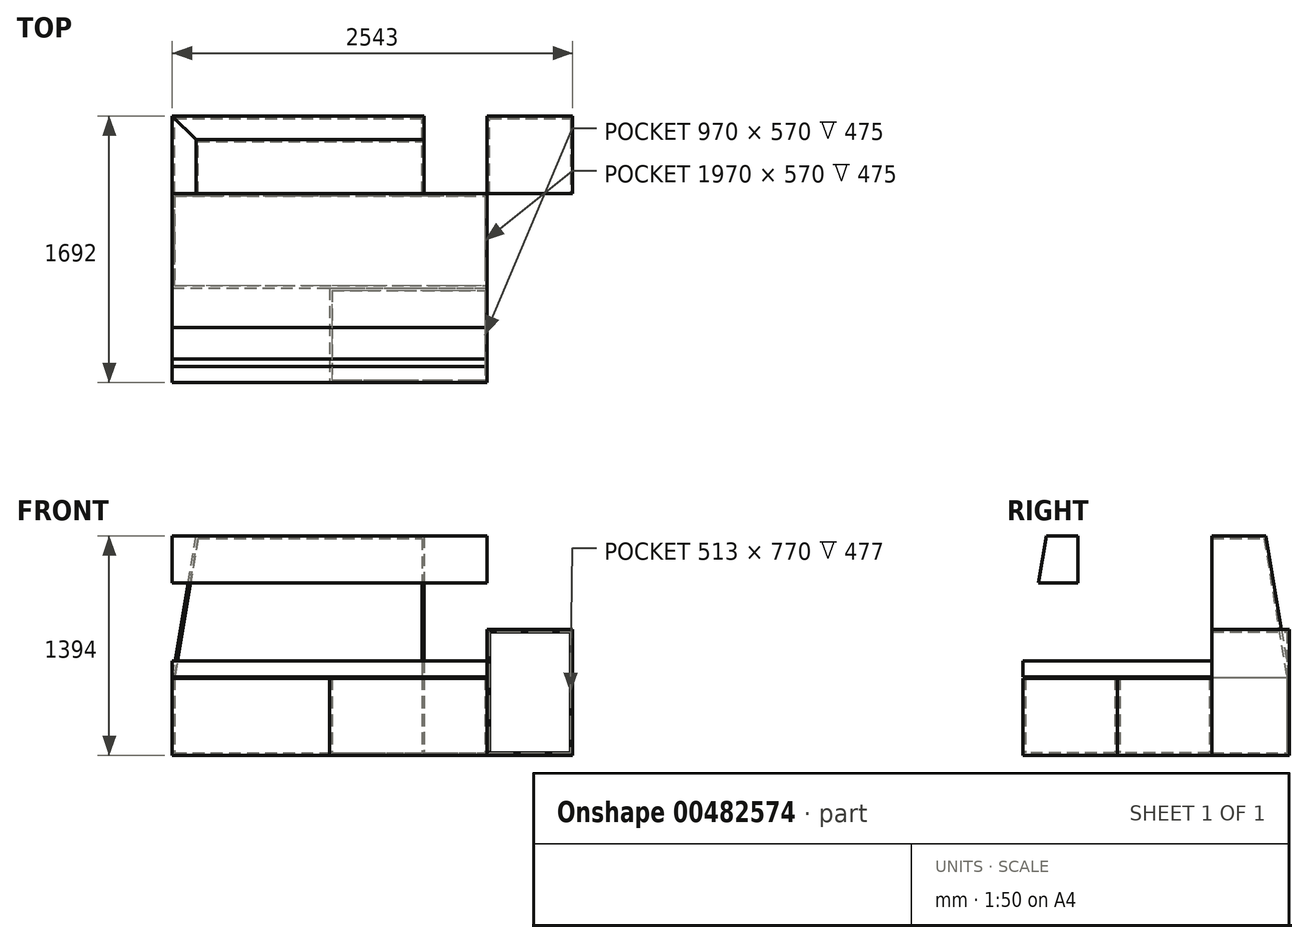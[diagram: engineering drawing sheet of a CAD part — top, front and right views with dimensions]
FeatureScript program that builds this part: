
annotation { "Feature Type Name" : "Feature", "Feature Type Description" : "" }
export const myFeature = defineFeature(function(context is Context, id is Id, definition is map)
    precondition{}
    {
        {
            var Q0;
            Q0=qCreatedBy(makeId("Top.planeOp"),FACE);
            var sketch = newSketch(context, id + "F0", { "sketchPlane" : qUnion([Q0])});
            skLineSegment(sketch, "E0.bottom", {"start": v(1471.5, -846) * mm, "end": v(-1471.5, -846) * mm, "construction": true});
            skLineSegment(sketch, "E0.top", {"start": v(1471.5, 846) * mm, "end": v(-1471.5, 846) * mm, "construction": true});
            skLineSegment(sketch, "E0.left", {"start": v(1471.5, -846) * mm, "end": v(1471.5, 846) * mm, "construction": true});
            skLineSegment(sketch, "E0.right", {"start": v(-1471.5, -846) * mm, "end": v(-1471.5, 846) * mm, "construction": true});
            skLineSegment(sketch, "E1", {"start": v(1071.5, 846) * mm, "end": v(1071.5, -846) * mm, "construction": true});
            skPoint(sketch, "E2", {"position": v(-1471.5, 622) * mm});
            skPoint(sketch, "E3", {"position": v(-1471.5, -622) * mm});
            skPoint(sketch, "E4", {"position": v(-1471.5, 0) * mm});
            skSolve(sketch);
        }
        {
            var Q0;
            Q0=qCreatedBy(makeId("Top.planeOp"),FACE);
            var sketch = newSketch(context, id + "F1", { "sketchPlane" : qUnion([Q0])});
            skLineSegment(sketch, "E5.bottom", {"start": v(-1471.5, 354) * mm, "end": v(528.5, 354) * mm});
            skLineSegment(sketch, "E5.top", {"start": v(-1471.5, -846) * mm, "end": v(528.5, -846) * mm});
            skLineSegment(sketch, "E5.left", {"start": v(-1471.5, 354) * mm, "end": v(-1471.5, -846) * mm});
            skLineSegment(sketch, "E5.right", {"start": v(528.5, 354) * mm, "end": v(528.5, -846) * mm});
            skLineSegment(sketch, "E6.top", {"start": v(-1471.5, 846) * mm, "end": v(528.5, 846) * mm});
            skLineSegment(sketch, "E6.left", {"start": v(-1471.5, 354) * mm, "end": v(-1471.5, 846) * mm});
            skLineSegment(sketch, "E6.right", {"start": v(528.5, 354) * mm, "end": v(528.5, 846) * mm});
            skLineSegment(sketch, "E7.left", {"start": v(-1471.5, -846) * mm, "end": v(-1471.5, -846) * mm});
            skLineSegment(sketch, "E7.right", {"start": v(528.5, -846) * mm, "end": v(528.5, -846) * mm});
            skLineSegment(sketch, "E8", {"start": v(-1471.5, -246) * mm, "end": v(528.5, -246) * mm});
            skLineSegment(sketch, "E9.bottom", {"start": v(528.5, 846) * mm, "end": v(1071.5, 846) * mm});
            skLineSegment(sketch, "E9.top", {"start": v(528.5, 354) * mm, "end": v(1071.5, 354) * mm});
            skLineSegment(sketch, "E9.left", {"start": v(528.5, 846) * mm, "end": v(528.5, 354) * mm});
            skLineSegment(sketch, "E9.right", {"start": v(1071.5, 846) * mm, "end": v(1071.5, 354) * mm});
            skLineSegment(sketch, "E10", {"start": v(-471.5, -246) * mm, "end": v(-471.5, -846) * mm});
            skLineSegment(sketch, "E11", {"start": v(128.5, 354) * mm, "end": v(128.5, 846) * mm});
            skSolve(sketch);
        }
        {
            var Q0;
            Q0=makeQuery(id+"F1.imprint","IMPRINT",FACE,{"disambiguationData":[TD([[makeQuery(id+"F1.imprint","IMPRINT",EDGE,{"derivedFrom":sQuery(id+"F1.wireOp",EDGE,"E5.left")}),1.0]])]});
            var Q1;
            {var subQ1=sQuery(id+"F1.wireOp",EDGE,"E5.right");var subQ3=sQuery(id+"F1.wireOp",EDGE,"E8");var subQ4=makeQuery(id+"F1.imprint","INTERSECT",VERTEX,{"derivedFrom":[subQ1,subQ3]});Q1=makeQuery(id+"F1.imprint","IMPRINT",FACE,{"disambiguationData":[TD([[makeQuery(id+"F1.imprint","IMPRINT",EDGE,{"disambiguationData":[TD([[subQ4,1.0]])],"derivedFrom":subQ3}),-1.0]])]});}
            var Q2;
            {var subQ4=sQuery(id+"F1.wireOp",EDGE,"E5.bottom");Q2=makeQuery(id+"F1.imprint","IMPRINT",FACE,{"disambiguationData":[TD([[makeQuery(id+"F1.imprint","IMPRINT",EDGE,{"derivedFrom":subQ4}),-1.0]])]});}
            extrude(context, id + "F2", {"entities" : qUnion([Q0, Q1, Q2]), "depth" : 600 * mm});
        }
        {
            var Q0;
            {var subQ0=sQuery(id+"F1.wireOp",EDGE,"E6.left");Q0=makeQuery(id+"F1.imprint","IMPRINT",FACE,{"disambiguationData":[TD([[makeQuery(id+"F1.imprint","IMPRINT",EDGE,{"derivedFrom":subQ0}),-1.0]])]});}
            extrude(context, id + "F3", {"entities" : qUnion([Q0]), "depth" : 1394 * mm});
        }
        {
            var Q0;
            {var subQ1=sQuery(id+"F1.wireOp",EDGE,"E5.left");var subQ3=sQuery(id+"F1.wireOp",EDGE,"E8");var subQ4=makeQuery(id+"F1.imprint","INTERSECT",VERTEX,{"derivedFrom":[subQ1,subQ3]});Q0=makeQuery(id+"F1.imprint","IMPRINT",FACE,{"disambiguationData":[TD([[makeQuery(id+"F1.imprint","IMPRINT",EDGE,{"disambiguationData":[TD([[subQ4,-1.0]])],"derivedFrom":subQ3}),-1.0]])]});}
            var Q1;
            {var subQ1=sQuery(id+"F1.wireOp",EDGE,"E5.right");var subQ3=sQuery(id+"F1.wireOp",EDGE,"E8");var subQ4=makeQuery(id+"F1.imprint","INTERSECT",VERTEX,{"derivedFrom":[subQ1,subQ3]});Q1=makeQuery(id+"F1.imprint","IMPRINT",FACE,{"disambiguationData":[TD([[makeQuery(id+"F1.imprint","IMPRINT",EDGE,{"disambiguationData":[TD([[subQ4,1.0]])],"derivedFrom":subQ3}),-1.0]])]});}
            var Q2;
            {var subQ4=sQuery(id+"F1.wireOp",EDGE,"E5.bottom");Q2=makeQuery(id+"F1.imprint","IMPRINT",FACE,{"disambiguationData":[TD([[makeQuery(id+"F1.imprint","IMPRINT",EDGE,{"derivedFrom":subQ4}),-1.0]])]});}
            extrude(context, id + "F4", {"entities" : qUnion([Q0, Q1, Q2]), "operationType" : NewBodyOperationType.REMOVE, "depth" : 500 * mm});
        }
        {
            var Q0;
            Q0=makeQuery(id+"F1.imprint","IMPRINT",FACE,{"disambiguationData":[TD([[makeQuery(id+"F1.imprint","IMPRINT",EDGE,{"derivedFrom":sQuery(id+"F1.wireOp",EDGE,"E9.bottom")}),-1.0]])]});
            var Q1;
            {var subQ0=sQuery(id+"F1.wireOp",EDGE,"E9.left");Q1=makeQuery(id+"F1.imprint","IMPRINT",FACE,{"disambiguationData":[TD([[makeQuery(id+"F1.imprint","IMPRINT",EDGE,{"derivedFrom":subQ0}),-1.0]])]});}
            extrude(context, id + "F5", {"entities" : qUnion([Q0, Q1]), "depth" : 800 * mm});
        }
        {
            var Q0;
            Q0=makeQuery(id+"F3.opExtrude","CAP_EDGE",EDGE,{"disambiguationData":[OSD([sQuery(id+"F1.wireOp",EDGE,"E6.top")])],"isStart":false});
            var Q1;
            Q1=makeQuery(id+"F3.opExtrude","CAP_EDGE",EDGE,{"disambiguationData":[OSD([sQuery(id+"F1.wireOp",EDGE,"E6.left")])],"isStart":false});
            chamfer(context, id + "F6", {"entities" : qUnion([Q0, Q1]), "chamferType" : ChamferType.TWO_OFFSETS, "width1" : 900 * mm, "oppositeDirection" : false, "width2" : 150 * mm, "tangentPropagation" : true});
        }
        {
            var Q0;
            {var subQ1=sQuery(id+"F1.wireOp",EDGE,"E5.right");var subQ3=sQuery(id+"F1.wireOp",EDGE,"E8");var subQ4=makeQuery(id+"F1.imprint","INTERSECT",VERTEX,{"derivedFrom":[subQ1,subQ3]});Q0=makeQuery(id+"F1.imprint","IMPRINT",FACE,{"disambiguationData":[TD([[makeQuery(id+"F1.imprint","IMPRINT",EDGE,{"disambiguationData":[TD([[subQ4,1.0]])],"derivedFrom":subQ3}),-1.0]])]});}
            extrude(context, id + "F7", {"entities" : qUnion([Q0]), "depth" : 490 * mm});
        }
        {
            var Q0;
            {var subQ0=sQuery(id+"F1.wireOp",EDGE,"E5.bottom");Q0=makeQuery(id+"F1.imprint","IMPRINT",FACE,{"disambiguationData":[TD([[makeQuery(id+"F1.imprint","IMPRINT",EDGE,{"derivedFrom":subQ0}),-1.0]])]});}
            extrude(context, id + "F8", {"entities" : qUnion([Q0]), "depth" : 490 * mm});
        }
        {
            var Q0;
            Q0=makeQuery(id+"F8.opExtrude","CAP_FACE",FACE,{"disambiguationData":[OSD([sQuery(id+"F1.wireOp",EDGE,"E5.left"),sQuery(id+"F1.wireOp",EDGE,"E5.right"),sQuery(id+"F1.wireOp",EDGE,"E6.top"),sQuery(id+"F1.wireOp",EDGE,"E6.left"),sQuery(id+"F1.wireOp",EDGE,"E8"),sQuery(id+"F1.wireOp",EDGE,"E9.left")])],"isStart":false});
            var Q1;
            Q1=makeQuery(id+"F7.opExtrude","CAP_FACE",FACE,{"disambiguationData":[OSD([sQuery(id+"F1.wireOp",EDGE,"E5.left"),sQuery(id+"F1.wireOp",EDGE,"E5.right"),sQuery(id+"F1.wireOp",EDGE,"E5.top"),sQuery(id+"F1.wireOp",EDGE,"E7.left"),sQuery(id+"F1.wireOp",EDGE,"E7.right"),sQuery(id+"F1.wireOp",EDGE,"E8")])],"isStart":false});
            var Q2;
            Q2=makeQuery(id+"F3.opExtrude","SWEPT_FACE",FACE,{"disambiguationData":[OSD([sQuery(id+"F1.wireOp",EDGE,"E5.top")])]});
            var Q3;
            Q3=makeQuery(id+"F3.opExtrude","SWEPT_FACE",FACE,{"disambiguationData":[OSD([sQuery(id+"F1.wireOp",EDGE,"E5.bottom")])]});
            var Q4;
            Q4=makeQuery(id+"F5.opExtrude","SWEPT_FACE",FACE,{"disambiguationData":[OSD([sQuery(id+"F1.wireOp",EDGE,"E9.top")])]});
            shell(context, id + "F9", {"entities" : qUnion([Q0, Q1, Q2, Q3, Q4]), "thickness" : 15 * mm});
        }
        {
            var Q0;
            Q0=qCreatedBy(makeId("Top.planeOp"),FACE);
            cPlane(context, id + "F10", {"entities" : qUnion([Q0]), "cplaneType" : CPlaneType.OFFSET, "offset" : 1394 * mm, "width" : 150 * mm, "height" : 150 * mm});
        }
        {
            var Q0;
            Q0=qCreatedBy(id+"F10.planeOp",FACE);
            var sketch = newSketch(context, id + "F11", { "sketchPlane" : qUnion([Q0])});
            skLineSegment(sketch, "E12.bottom", {"start": v(-1471.5, 846) * mm, "end": v(1471.5, 846) * mm, "construction": true});
            skLineSegment(sketch, "E12.top", {"start": v(-1471.5, -846) * mm, "end": v(1471.5, -846) * mm, "construction": true});
            skLineSegment(sketch, "E12.left", {"start": v(-1471.5, 846) * mm, "end": v(-1471.5, -846) * mm, "construction": true});
            skLineSegment(sketch, "E12.right", {"start": v(1471.5, 846) * mm, "end": v(1471.5, -846) * mm, "construction": true});
            skLineSegment(sketch, "E13", {"start": v(1071.5, 846) * mm, "end": v(1071.5, -846) * mm, "construction": true});
            skLineSegment(sketch, "E14.bottom", {"start": v(-1471.5, -846) * mm, "end": v(528.5, -846) * mm});
            skLineSegment(sketch, "E14.top", {"start": v(-1471.5, -496) * mm, "end": v(528.5, -496) * mm});
            skLineSegment(sketch, "E14.left", {"start": v(-1471.5, -846) * mm, "end": v(-1471.5, -496) * mm});
            skLineSegment(sketch, "E14.right", {"start": v(528.5, -846) * mm, "end": v(528.5, -496) * mm});
            skSolve(sketch);
        }
        {
            var Q0;
            Q0=makeQuery(id+"F11.imprint","IMPRINT",FACE,{"disambiguationData":[TD([[makeQuery(id+"F11.imprint","IMPRINT",EDGE,{"derivedFrom":sQuery(id+"F11.wireOp",EDGE,"E14.bottom")}),1.0]])]});
            extrude(context, id + "F12", {"entities" : qUnion([Q0]), "oppositeDirection" : true, "depth" : 300 * mm});
        }
        {
            var Q0;
            Q0=makeQuery(id+"F12.opExtrude","CAP_EDGE",EDGE,{"disambiguationData":[OSD([sQuery(id+"F11.wireOp",EDGE,"E14.bottom")])],"isStart":true});
            chamfer(context, id + "F13", {"entities" : qUnion([Q0]), "chamferType" : ChamferType.TWO_OFFSETS, "width1" : 150 * mm, "oppositeDirection" : false, "width2" : 900 * mm, "tangentPropagation" : true});
        }
    });
